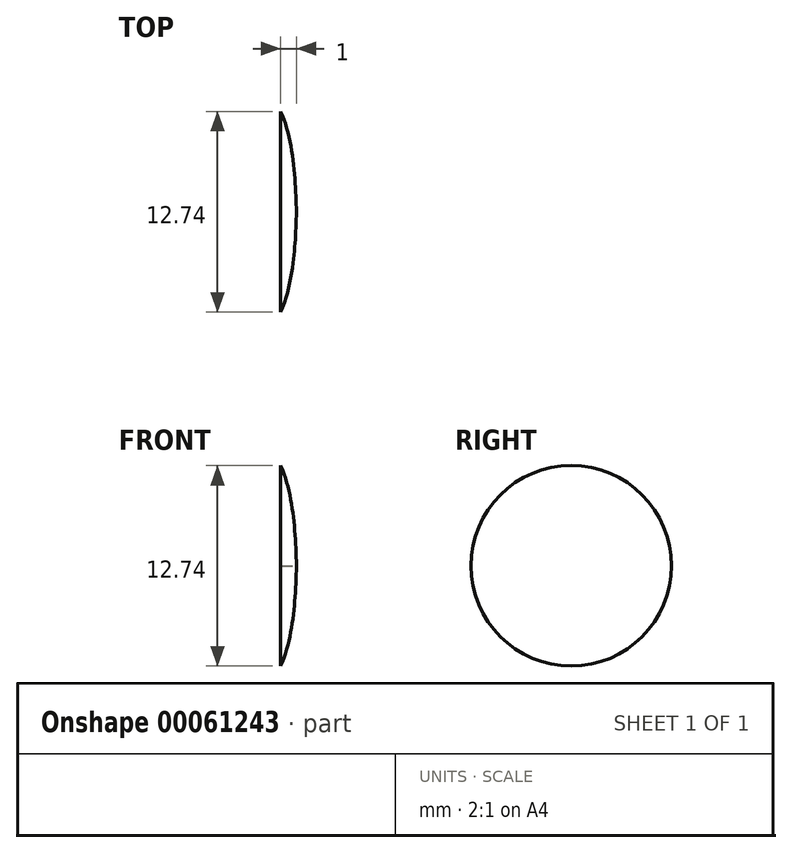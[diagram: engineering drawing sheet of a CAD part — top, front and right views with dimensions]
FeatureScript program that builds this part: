
annotation { "Feature Type Name" : "Feature", "Feature Type Description" : "" }
export const myFeature = defineFeature(function(context is Context, id is Id, definition is map)
    precondition{}
    {
        {
            var Q0;
            Q0=qCreatedBy(makeId("Top.planeOp"),FACE);
            var sketch = newSketch(context, id + "F0", { "sketchPlane" : qUnion([Q0])});
            skLineSegment(sketch, "E0", {"start": v(0, 6.37) * mm, "end": v(0, 0) * mm});
            skLineSegment(sketch, "E1", {"start": v(1, 0) * mm, "end": v(0, 0) * mm});
            skPoint(sketch, "E2.center.orphan", {"position": v(-4.67, 0) * mm});
            skFitSpline(sketch, "E3", {"points": [v(0, 6.37) * mm, v(1, 0) * mm], "startDerivative": vector(2.54, -5.66) * mm, "endDerivative": vector(0.12, -5.25) * mm});
            skPoint(sketch, "E4.orphan", {"position": v(2, 0) * mm});
            skSolve(sketch);
        }
        {
            var Q0;
            Q0=makeQuery(id+"F0.imprint","IMPRINT",FACE,{"disambiguationData":[TD([[makeQuery(id+"F0.imprint","IMPRINT",EDGE,{"derivedFrom":sQuery(id+"F0.wireOp",EDGE,"E0")}),1.0]])]});
            var Q1;
            Q1=sQuery(id+"F0.wireOp",EDGE,"E1");
            revolve(context, id + "F1", {"entities" : qUnion([Q0]), "axis" : qUnion([Q1]), "revolveType" : RevolveType.FULL});
        }
    });
